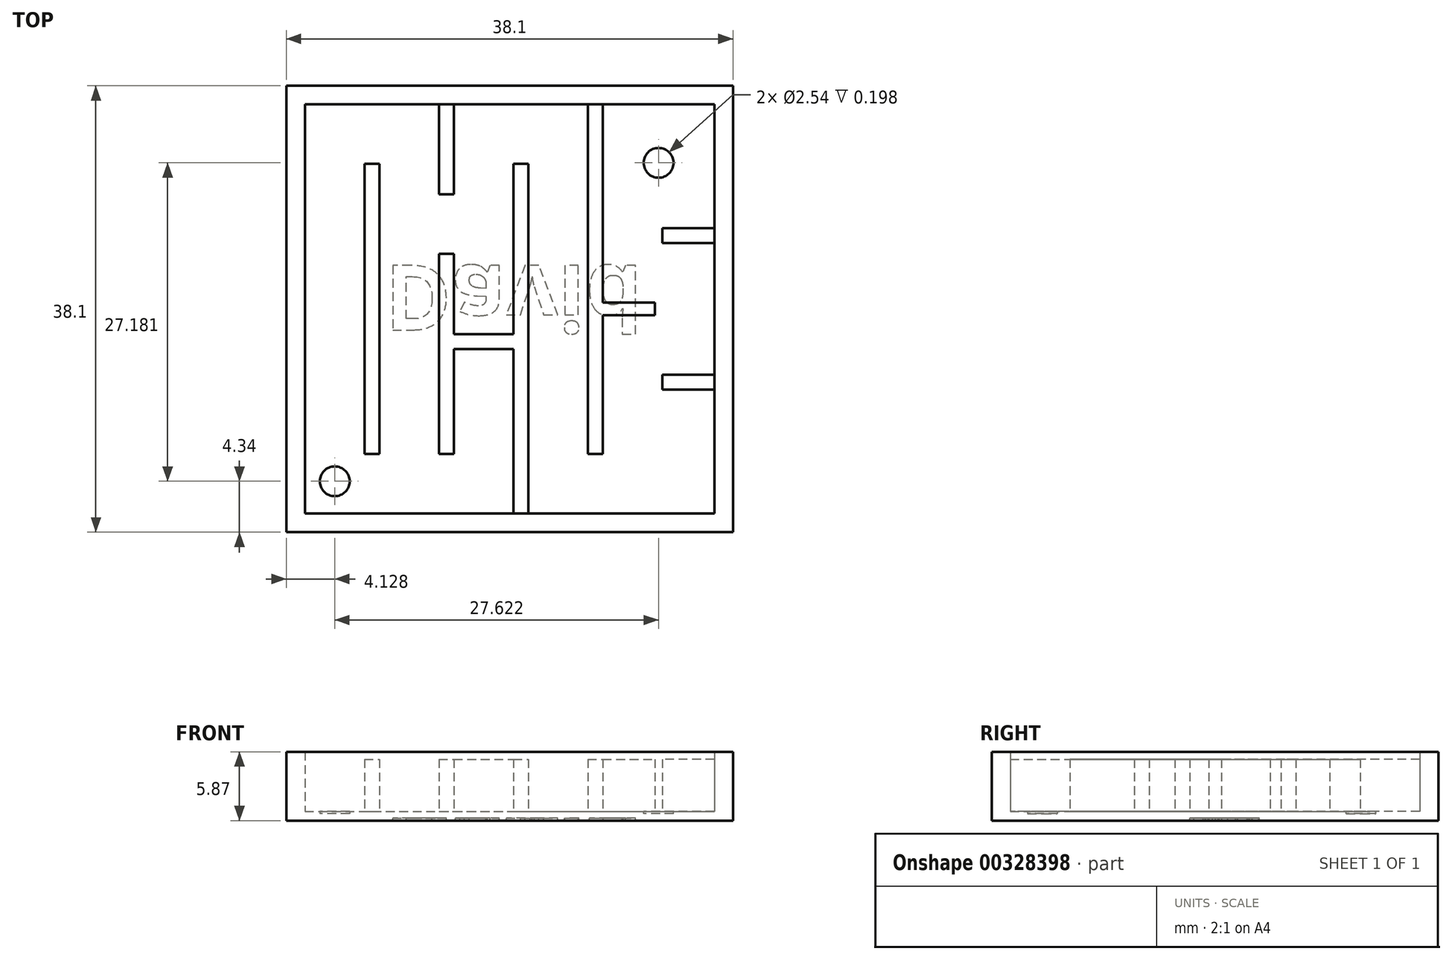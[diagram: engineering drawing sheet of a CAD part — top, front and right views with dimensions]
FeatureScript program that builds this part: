
annotation { "Feature Type Name" : "Feature", "Feature Type Description" : "" }
export const myFeature = defineFeature(function(context is Context, id is Id, definition is map)
    precondition{}
    {
        {
            var Q0;
            Q0=qCreatedBy(makeId("Top.planeOp"),FACE);
            var sketch = newSketch(context, id + "F0", { "sketchPlane" : qUnion([Q0])});
            skLineSegment(sketch, "E0.bottom", {"start": v(-19.05, 13.38) * mm, "end": v(19.05, 13.38) * mm});
            skLineSegment(sketch, "E0.top", {"start": v(-19.05, -24.72) * mm, "end": v(19.05, -24.72) * mm});
            skLineSegment(sketch, "E0.left", {"start": v(-19.05, 13.38) * mm, "end": v(-19.05, -24.72) * mm});
            skLineSegment(sketch, "E0.right", {"start": v(19.05, 13.38) * mm, "end": v(19.05, -24.72) * mm});
            skSolve(sketch);
        }
        {
            var Q0;
            Q0=makeQuery(id+"F0.imprint","IMPRINT",FACE,{"disambiguationData":[TD([[makeQuery(id+"F0.imprint","IMPRINT",EDGE,{"derivedFrom":sQuery(id+"F0.wireOp",EDGE,"E0.bottom")}),-1.0]])]});
            extrude(context, id + "F1", {"entities" : qUnion([Q0]), "depth" : 0.8 * mm});
        }
        {
            var Q0;
            Q0=makeQuery(id+"F1.opExtrude","CAP_FACE",FACE,{"disambiguationData":[OSD([sQuery(id+"F0.wireOp",EDGE,"E0.bottom"),sQuery(id+"F0.wireOp",EDGE,"E0.top"),sQuery(id+"F0.wireOp",EDGE,"E0.left"),sQuery(id+"F0.wireOp",EDGE,"E0.right")])],"isStart":false});
            var sketch = newSketch(context, id + "F2", { "sketchPlane" : qUnion([Q0])});
            skLineSegment(sketch, "E1.0", {"start": v(-17.46, 11.8) * mm, "end": v(17.46, 11.8) * mm});
            skLineSegment(sketch, "E1.1", {"start": v(-17.46, 11.8) * mm, "end": v(-17.46, -23.13) * mm});
            skLineSegment(sketch, "E1.2", {"start": v(-17.46, -23.13) * mm, "end": v(17.46, -23.13) * mm});
            skLineSegment(sketch, "E1.3", {"start": v(17.46, 11.8) * mm, "end": v(17.46, -23.13) * mm});
            skSolve(sketch);
        }
        {
            var Q0;
            Q0=makeQuery(id+"F2.imprint","IMPRINT",FACE,{"disambiguationData":[TD([[makeQuery(id+"F2.imprint","IMPRINT",EDGE,{"derivedFrom":sQuery(id+"F2.wireOp",EDGE,"E1.0")}),1.0]])]});
            extrude(context, id + "F3", {"entities" : qUnion([Q0]), "operationType" : NewBodyOperationType.ADD, "depth" : 5.08 * mm});
        }
        {
            var Q0;
            Q0=makeQuery(id+"F1.opExtrude","CAP_FACE",FACE,{"disambiguationData":[OSD([sQuery(id+"F0.wireOp",EDGE,"E0.bottom"),sQuery(id+"F0.wireOp",EDGE,"E0.top"),sQuery(id+"F0.wireOp",EDGE,"E0.left"),sQuery(id+"F0.wireOp",EDGE,"E0.right")])],"isStart":false});
            var sketch = newSketch(context, id + "F4", { "sketchPlane" : qUnion([Q0])});
            skLineSegment(sketch, "E2.bottom", {"start": v(-12.38, -23.13) * mm, "end": v(-11.11, -23.13) * mm});
            skLineSegment(sketch, "E2.top", {"start": v(-12.38, 6.71) * mm, "end": v(-11.11, 6.71) * mm});
            skLineSegment(sketch, "E2.left", {"start": v(-12.38, -18.05) * mm, "end": v(-12.38, 6.71) * mm});
            skLineSegment(sketch, "E2.right", {"start": v(-11.11, -18.05) * mm, "end": v(-11.11, 6.71) * mm});
            skLineSegment(sketch, "E3.bottom", {"start": v(-6.03, 11.8) * mm, "end": v(-4.76, 11.8) * mm});
            skLineSegment(sketch, "E3.top", {"start": v(-6.03, -18.05) * mm, "end": v(-4.76, -18.05) * mm});
            skLineSegment(sketch, "E3.left", {"start": v(-6.03, 11.8) * mm, "end": v(-6.03, 4.11) * mm});
            skLineSegment(sketch, "E3.right", {"start": v(-4.76, 11.8) * mm, "end": v(-4.76, 4.11) * mm});
            skLineSegment(sketch, "E4.bottom", {"start": v(0.32, -23.13) * mm, "end": v(1.59, -23.13) * mm});
            skLineSegment(sketch, "E4.top", {"start": v(0.32, 6.71) * mm, "end": v(1.59, 6.71) * mm});
            skLineSegment(sketch, "E4.left", {"start": v(0.32, -23.13) * mm, "end": v(0.32, 6.71) * mm});
            skLineSegment(sketch, "E4.right", {"start": v(1.59, -23.13) * mm, "end": v(1.59, 6.71) * mm});
            skLineSegment(sketch, "E5.bottom", {"start": v(6.67, 11.8) * mm, "end": v(7.94, 11.8) * mm});
            skLineSegment(sketch, "E5.top", {"start": v(6.67, -18.05) * mm, "end": v(7.94, -18.05) * mm});
            skLineSegment(sketch, "E5.left", {"start": v(6.67, 11.8) * mm, "end": v(6.67, -18.05) * mm});
            skLineSegment(sketch, "E5.right", {"start": v(7.94, 11.8) * mm, "end": v(7.94, -18.05) * mm});
            skLineSegment(sketch, "E6.bottom", {"start": v(-4.76, -7.8) * mm, "end": v(0.32, -7.8) * mm});
            skLineSegment(sketch, "E6.top", {"start": v(-4.76, -9.08) * mm, "end": v(0.32, -9.08) * mm});
            skLineSegment(sketch, "E6.left", {"start": v(-4.76, -7.8) * mm, "end": v(-4.76, -9.08) * mm});
            skLineSegment(sketch, "E6.right", {"start": v(0.32, -7.8) * mm, "end": v(0.32, -9.08) * mm});
            skPoint(sketch, "E7.start.orphan", {"position": v(-11.11, -18.05) * mm});
            skPoint(sketch, "E8.start.orphan", {"position": v(-12.38, -18.05) * mm});
            skLineSegment(sketch, "E9", {"start": v(-12.38, -18.05) * mm, "end": v(-11.11, -18.05) * mm});
            skLineSegment(sketch, "E10.bottom", {"start": v(-6.03, 4.74) * mm, "end": v(-4.76, 4.74) * mm});
            skLineSegment(sketch, "E10.top", {"start": v(-6.03, 4.11) * mm, "end": v(-4.76, 4.11) * mm});
            skLineSegment(sketch, "E10.left", {"start": v(-6.03, 4.74) * mm, "end": v(-6.03, 4.11) * mm});
            skLineSegment(sketch, "E10.right", {"start": v(-4.76, 4.74) * mm, "end": v(-4.76, 4.11) * mm});
            skLineSegment(sketch, "E11.top", {"start": v(-6.03, -0.97) * mm, "end": v(-4.76, -0.97) * mm});
            skLineSegment(sketch, "E12.trimOffspring", {"start": v(-4.76, -0.97) * mm, "end": v(-4.76, -18.05) * mm});
            skLineSegment(sketch, "E13.trimOffspring", {"start": v(-6.03, -0.97) * mm, "end": v(-6.03, -18.05) * mm});
            skLineSegment(sketch, "E14.bottom", {"start": v(17.46, -11.27) * mm, "end": v(13.02, -11.27) * mm});
            skLineSegment(sketch, "E14.top", {"start": v(17.46, -12.54) * mm, "end": v(13.02, -12.54) * mm});
            skLineSegment(sketch, "E14.left", {"start": v(17.46, -11.27) * mm, "end": v(17.46, -12.54) * mm});
            skLineSegment(sketch, "E14.right", {"start": v(13.02, -11.27) * mm, "end": v(13.02, -12.54) * mm});
            skLineSegment(sketch, "E15.bottom", {"start": v(7.94, -5.12) * mm, "end": v(12.38, -5.12) * mm});
            skLineSegment(sketch, "E15.top", {"start": v(7.94, -6.2) * mm, "end": v(12.38, -6.2) * mm});
            skLineSegment(sketch, "E15.left", {"start": v(7.94, -5.12) * mm, "end": v(7.94, -6.2) * mm});
            skLineSegment(sketch, "E16", {"start": v(12.38, -5.12) * mm, "end": v(12.38, -6.2) * mm});
            skPoint(sketch, "E17.orphan", {"position": v(13.02, -6.2) * mm});
            skLineSegment(sketch, "E18.bottom", {"start": v(17.46, 1.23) * mm, "end": v(13.02, 1.23) * mm});
            skLineSegment(sketch, "E18.top", {"start": v(17.46, -0.04) * mm, "end": v(13.02, -0.04) * mm});
            skLineSegment(sketch, "E18.left", {"start": v(17.46, 1.23) * mm, "end": v(17.46, -0.04) * mm});
            skLineSegment(sketch, "E18.right", {"start": v(13.02, 1.23) * mm, "end": v(13.02, -0.04) * mm});
            skSolve(sketch);
        }
        {
            var Q0;
            Q0=makeQuery(id+"F4.imprint","IMPRINT",FACE,{"disambiguationData":[TD([[makeQuery(id+"F4.imprint","IMPRINT",EDGE,{"derivedFrom":sQuery(id+"F4.wireOp",EDGE,"E2.top")}),-1.0]])]});
            var Q1;
            {var subQ4=sQuery(id+"F4.wireOp",EDGE,"E3.top");Q1=makeQuery(id+"F4.imprint","IMPRINT",FACE,{"disambiguationData":[TD([[makeQuery(id+"F4.imprint","IMPRINT",EDGE,{"derivedFrom":subQ4}),1.0]])]});}
            var Q2;
            Q2=makeQuery(id+"F4.imprint","IMPRINT",FACE,{"disambiguationData":[TD([[makeQuery(id+"F4.imprint","IMPRINT",EDGE,{"derivedFrom":sQuery(id+"F4.wireOp",EDGE,"E3.bottom")}),-1.0]])]});
            var Q3;
            Q3=makeQuery(id+"F4.imprint","IMPRINT",FACE,{"disambiguationData":[TD([[makeQuery(id+"F4.imprint","IMPRINT",EDGE,{"derivedFrom":sQuery(id+"F4.wireOp",EDGE,"E10.top")}),1.0]])]});
            var Q4;
            {var subQ3=sQuery(id+"F4.wireOp",EDGE,"E4.bottom");Q4=makeQuery(id+"F4.imprint","IMPRINT",FACE,{"disambiguationData":[TD([[makeQuery(id+"F4.imprint","IMPRINT",EDGE,{"derivedFrom":subQ3}),1.0]])]});}
            var Q5;
            {var subQ0=sQuery(id+"F4.wireOp",EDGE,"E6.bottom");Q5=makeQuery(id+"F4.imprint","IMPRINT",FACE,{"disambiguationData":[TD([[makeQuery(id+"F4.imprint","IMPRINT",EDGE,{"derivedFrom":subQ0}),-1.0]])]});}
            var Q6;
            {var subQ1=sQuery(id+"F4.wireOp",EDGE,"E5.bottom");Q6=makeQuery(id+"F4.imprint","IMPRINT",FACE,{"disambiguationData":[TD([[makeQuery(id+"F4.imprint","IMPRINT",EDGE,{"derivedFrom":subQ1}),-1.0]])]});}
            var Q7;
            Q7=makeQuery(id+"F4.imprint","IMPRINT",FACE,{"disambiguationData":[TD([[makeQuery(id+"F4.imprint","IMPRINT",EDGE,{"derivedFrom":sQuery(id+"F4.wireOp",EDGE,"E15.bottom")}),-1.0]])]});
            var Q8;
            Q8=makeQuery(id+"F4.imprint","IMPRINT",FACE,{"disambiguationData":[TD([[makeQuery(id+"F4.imprint","IMPRINT",EDGE,{"derivedFrom":sQuery(id+"F4.wireOp",EDGE,"E18.bottom")}),1.0]])]});
            var Q9;
            Q9=makeQuery(id+"F4.imprint","IMPRINT",FACE,{"disambiguationData":[TD([[makeQuery(id+"F4.imprint","IMPRINT",EDGE,{"derivedFrom":sQuery(id+"F4.wireOp",EDGE,"E14.bottom")}),1.0]])]});
            extrude(context, id + "F5", {"entities" : qUnion([Q0, Q1, Q2, Q3, Q4, Q5, Q6, Q7, Q8, Q9]), "operationType" : NewBodyOperationType.ADD, "depth" : 4.44 * mm});
        }
        {
            var Q0;
            Q0=makeQuery(id+"F1.opExtrude","CAP_FACE",FACE,{"disambiguationData":[OSD([sQuery(id+"F0.wireOp",EDGE,"E0.bottom"),sQuery(id+"F0.wireOp",EDGE,"E0.top"),sQuery(id+"F0.wireOp",EDGE,"E0.left"),sQuery(id+"F0.wireOp",EDGE,"E0.right")])],"isStart":true});
            var sketch = newSketch(context, id + "F6", { "sketchPlane" : qUnion([Q0])});
            skText(sketch, "E19", { "text": "David", "fontName": "OpenSans-Bold.ttf"});
            skLineSegment(sketch, "E20.0", {"start": v(-19.05, 18.37) * mm, "end": v(19.05, 18.37) * mm});
            skLineSegment(sketch, "E21.0", {"start": v(-12.7, -13.38) * mm, "end": v(-12.7, 24.72) * mm});
            skLineSegment(sketch, "E22.0", {"start": v(25.4, -13.38) * mm, "end": v(25.4, 24.72) * mm});
            skLineSegment(sketch, "E23.0", {"start": v(-19.05, -19.73) * mm, "end": v(19.05, -19.73) * mm});
            const initialGuessF6  = {"E19": [-0.01067, 0.00195, 1, 0, 0.00556]};
            skSetInitialGuess(sketch, initialGuessF6);
            skSolve(sketch);
        }
        {
            var Q0;
            Q0 = qSketchRegion(id + "F6", true);
            extrude(context, id + "F7", {"entities" : qUnion([Q0]), "operationType" : NewBodyOperationType.REMOVE, "endBound" : BoundingType.SYMMETRIC, "depth" : 0.4 * mm});
        }
        {
            var Q0;
            Q0=makeQuery(id+"F1.opExtrude","CAP_FACE",FACE,{"disambiguationData":[OSD([sQuery(id+"F0.wireOp",EDGE,"E0.bottom"),sQuery(id+"F0.wireOp",EDGE,"E0.top"),sQuery(id+"F0.wireOp",EDGE,"E0.left"),sQuery(id+"F0.wireOp",EDGE,"E0.right")])],"isStart":false});
            var sketch = newSketch(context, id + "F8", { "sketchPlane" : qUnion([Q0])});
            skCircle(sketch, "E24", {"center": v(-14.92, -20.38) * mm, "radius": 1.27 * mm});
            skPoint(sketch, "E24.centerSnap0", {"position": v(-14.92, -18.05) * mm});
            skPoint(sketch, "E25.orphan", {"position": v(-12.38, -18.05) * mm});
            skPoint(sketch, "E26.end.orphan", {"position": v(-17.46, -18.05) * mm});
            skSolve(sketch);
        }
        {
            var Q0;
            Q0=makeQuery(id+"F8.imprint","IMPRINT",FACE,{"disambiguationData":[TD([[makeQuery(id+"F8.imprint","IMPRINT",EDGE,{"derivedFrom":sQuery(id+"F8.wireOp",EDGE,"E24")}),1.0]])]});
            extrude(context, id + "F9", {"entities" : qUnion([Q0]), "operationType" : NewBodyOperationType.REMOVE, "endBound" : BoundingType.SYMMETRIC, "depth" : 0.4 * mm});
        }
        {
            var Q0;
            Q0=makeQuery(id+"F1.opExtrude","CAP_FACE",FACE,{"disambiguationData":[OSD([sQuery(id+"F0.wireOp",EDGE,"E0.bottom"),sQuery(id+"F0.wireOp",EDGE,"E0.top"),sQuery(id+"F0.wireOp",EDGE,"E0.left"),sQuery(id+"F0.wireOp",EDGE,"E0.right")])],"isStart":false});
            var sketch = newSketch(context, id + "F10", { "sketchPlane" : qUnion([Q0])});
            skCircle(sketch, "E27", {"center": v(12.7, 6.8) * mm, "radius": 1.27 * mm});
            skPoint(sketch, "E27.centerSnap0", {"position": v(12.7, 11.8) * mm});
            skSolve(sketch);
        }
        {
            var Q0;
            Q0=makeQuery(id+"F10.imprint","IMPRINT",FACE,{"disambiguationData":[TD([[makeQuery(id+"F10.imprint","IMPRINT",EDGE,{"derivedFrom":sQuery(id+"F10.wireOp",EDGE,"E27")}),1.0]])]});
            extrude(context, id + "F11", {"entities" : qUnion([Q0]), "operationType" : NewBodyOperationType.REMOVE, "endBound" : BoundingType.SYMMETRIC, "oppositeDirection" : true, "depth" : 0.4 * mm});
        }
    });
